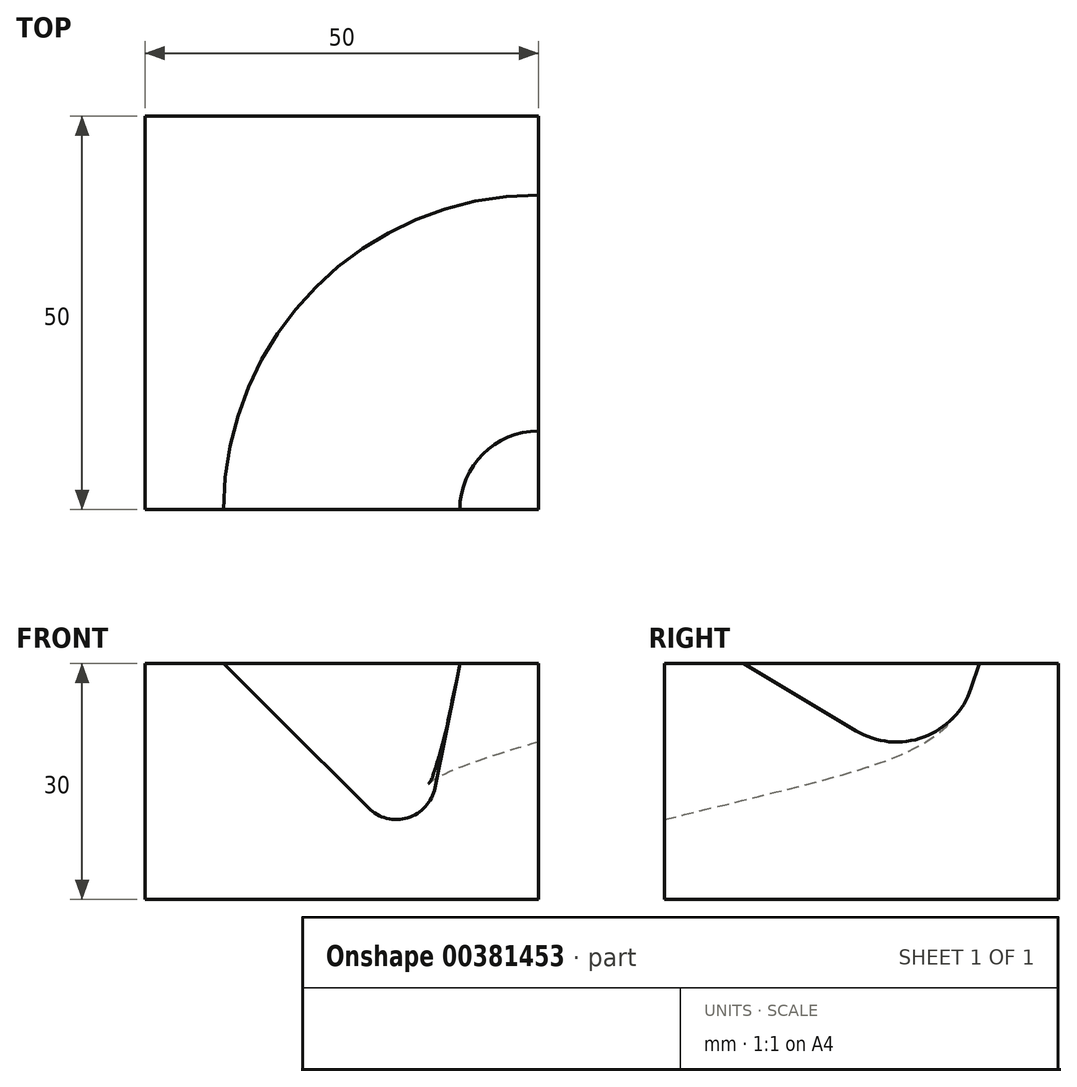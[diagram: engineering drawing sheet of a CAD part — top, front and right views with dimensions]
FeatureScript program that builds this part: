
annotation { "Feature Type Name" : "Feature", "Feature Type Description" : "" }
export const myFeature = defineFeature(function(context is Context, id is Id, definition is map)
    precondition{}
    {
        {
            var Q0;
            Q0=qCreatedBy(makeId("Top.planeOp"),FACE);
            var sketch = newSketch(context, id + "F0", { "sketchPlane" : qUnion([Q0])});
            skLineSegment(sketch, "E0.bottom", {"start": v(25, 25) * mm, "end": v(-25, 25) * mm});
            skLineSegment(sketch, "E0.top", {"start": v(25, -25) * mm, "end": v(-25, -25) * mm});
            skLineSegment(sketch, "E0.left", {"start": v(25, 25) * mm, "end": v(25, -25) * mm});
            skLineSegment(sketch, "E0.right", {"start": v(-25, 25) * mm, "end": v(-25, -25) * mm});
            skPoint(sketch, "E0.middle", {"position": v(0, 0) * mm});
            skSolve(sketch);
        }
        {
            var Q0;
            Q0=makeQuery(id+"F0.imprint","IMPRINT",FACE,{"disambiguationData":[TD([[makeQuery(id+"F0.imprint","IMPRINT",EDGE,{"derivedFrom":sQuery(id+"F0.wireOp",EDGE,"E0.bottom")}),1.0]])]});
            extrude(context, id + "F1", {"entities" : qUnion([Q0]), "depth" : 30 * mm});
        }
        {
            var Q0;
            Q0=makeQuery(id+"F1.opExtrude","SWEPT_FACE",FACE,{"disambiguationData":[OSD([sQuery(id+"F0.wireOp",EDGE,"E0.left")])]});
            var sketch = newSketch(context, id + "F2", { "sketchPlane" : qUnion([Q0])});
            skPoint(sketch, "E1", {"position": v(10, 15) * mm});
            skLineSegment(sketch, "E2", {"start": v(-15, 30) * mm, "end": v(-0.69, 21.41) * mm});
            skLineSegment(sketch, "E3", {"start": v(13.94, 26.83) * mm, "end": v(15, 30) * mm});
            skArc(sketch, "E4.filletArc", {"start": v(-0.69, 21.41) * mm, "mid": v(7.92, 20.6) * mm, "end": v(13.94, 26.83) * mm});
            skSolve(sketch);
        }
        {
            var Q0;
            Q0=makeQuery(id+"F1.opExtrude","SWEPT_FACE",FACE,{"disambiguationData":[OSD([sQuery(id+"F0.wireOp",EDGE,"E0.top")])]});
            var sketch = newSketch(context, id + "F3", { "sketchPlane" : qUnion([Q0])});
            skPoint(sketch, "E5", {"position": v(10, 5) * mm});
            skLineSegment(sketch, "E6", {"start": v(-15, 30) * mm, "end": v(3.4, 11.6) * mm});
            skLineSegment(sketch, "E7", {"start": v(11.83, 14.16) * mm, "end": v(15, 30) * mm});
            skArc(sketch, "E8.filletArc", {"start": v(3.4, 11.6) * mm, "mid": v(8.38, 10.36) * mm, "end": v(11.83, 14.16) * mm});
            skSolve(sketch);
        }
        {
            var Q0;
            Q0=makeQuery(id+"F1.opExtrude","CAP_FACE",FACE,{"disambiguationData":[OSD([sQuery(id+"F0.wireOp",EDGE,"E0.bottom"),sQuery(id+"F0.wireOp",EDGE,"E0.top"),sQuery(id+"F0.wireOp",EDGE,"E0.left"),sQuery(id+"F0.wireOp",EDGE,"E0.right")])],"isStart":false});
            var sketch = newSketch(context, id + "F4", { "sketchPlane" : qUnion([Q0])});
            skArc(sketch, "E9", {"start": v(15, -25) * mm, "mid": v(17.93, -17.93) * mm, "end": v(25, -15) * mm});
            skArc(sketch, "E10", {"start": v(-15, -25) * mm, "mid": v(-3.28, 3.28) * mm, "end": v(25, 15) * mm});
            skSolve(sketch);
        }
        {
            var Q1;
            {var subQ0=sQuery(id+"F2.wireOp",EDGE,"E2");Q1=makeQuery(id+"F2.imprint","IMPRINT",FACE,{"disambiguationData":[TD([[makeQuery(id+"F2.imprint","IMPRINT",EDGE,{"derivedFrom":subQ0}),1.0]])]});}
            var Q2;
            {var subQ0=sQuery(id+"F3.wireOp",EDGE,"E6");Q2=makeQuery(id+"F3.imprint","IMPRINT",FACE,{"disambiguationData":[TD([[makeQuery(id+"F3.imprint","IMPRINT",EDGE,{"derivedFrom":subQ0}),1.0]])]});}
            var Q3;
            Q3=sQuery(id+"F4.wireOp",EDGE,"E9");
            var Q4;
            Q4=sQuery(id+"F4.wireOp",EDGE,"E10");
            loft(context, id + "F5", {"operationType" : NewBodyOperationType.REMOVE, "addGuides" : true, "sheetProfilesArray" : [{ "sheetProfileEntities" : qUnion([Q1]) }, { "sheetProfileEntities" : qUnion([Q2]) }], "guidesArray" : [{ "guideEntities" : qUnion([Q3]), "guideDerivativeType" : LoftGuideDerivativeType.DEFAULT, "guideDerivativeMagnitude" : 1 }, { "guideEntities" : qUnion([Q4]), "guideDerivativeType" : LoftGuideDerivativeType.DEFAULT, "guideDerivativeMagnitude" : 1 }]});
        }
    });
